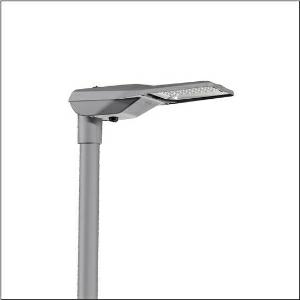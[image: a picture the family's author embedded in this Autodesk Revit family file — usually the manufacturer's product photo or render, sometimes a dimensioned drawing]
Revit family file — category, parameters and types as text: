
# Revit family: streetlight_sl_21_iq_mini___st1_0a_5xe2d41y08hb_48d2
name_source: partatom
category: Lighting Fixtures
units: mm (PartAtom-declared; Revit-internal decimal feet)

## family parameters
Cut with Voids When Loaded = No
Host = Face
Light Source = No
Part Type = Normal
Room Calculation Point = No
Round Connector Dimension = Use Diameter
Shared = No

## types (1)
- --- (1 x LED, 10080 lm, 71 W, 4000K)
    Apparent Load = 71 VA
    CIE Flux Codes = 37 72 97 100 100
    Color Rendering = 70
    Color Temperature = 4000K
    Default Elevation = 1800 mm
    Description = Streetlight SL 21 iQ mini, mast luminaire, primary light control with lens, of PMMA, primary optical cover: cover, of toughened safety glass, transparent, light distribution: ST1.0a, light emission: direct distribution, primary light characteristic: asymmetric, installation type: post-top, side-entry, LED, High Power LED, rated luminous flux: 10.080lm, luminous efficacy: 142lm/W, light colour: 740, colour temperature: 4000K, control gear: iQ-Street Remote, D4i with power reduction, control: pre-setting: logarithmic dimming characteristic, Street-Remote, Auto-Match, Temp-Guard, Lumen-Switch, Night-Set, Smart-Wire, Light-Fading, Desk-Remote (wireless, voltage-free reading and setting of iQ features in the workshop via application-optimized NFC function/RFID function), optimised constant luminous flux control (CLO 2.0), mains connection: 220..240V, AC, 50/60Hz, start of lifetime: 71W, end of service life: 75W, reduction: 31W, luminaire housing, of diecast aluminium, powder-coated, Siteco® metallic grey (DB 702S), corrosivity category C5 mid according to DIN EN ISO 12944, please order mast flange separately, inclination adjustable: 0°, 5°, 10°, 15°, sealing non-destructively replaceable, multi-level sealing system, length: 628mm, width: 235mm, height: 110mm, mast flange for spigot size: 42mm (side-entry): 5XC10008XM4, 60/48mm (side-entry/post-top): 5XC10108XM2, 76/60mm (side-entry/post-top): 5XC10108XM1, mounting height: 4..8m, Smart Interface below and above, protection rating (complete): IP66, insulation class (complete): insulation class II (safety insulation), certification: CE, ENEC, ENEC+, VDE, impact resistance: IK10, permissible operating ambient temperature for outdoor applications: -40..+50°C, standard-compliant lighting for roads and squares, packaging unit: 1 piece

Light Distribution: ST1.0a
    Height = 110 mm
    Lamp = 1 x LED
    Lamp Light Flux = 10080 lm
    Lamp Power = 71 W
    Lamp count = 1
    Length = 625 mm
    Luminous efficacy = 142 lm/W
    Manufacturer = Siteco
    ModVariant = No
    Model = 5XE2D41Y08HB
    Number of Poles = 1
    OnlyDefault = Yes
    Power Factor = 1
    Product Name = Streetlight SL 21 iQ mini | ST1.0a
    Product group = mast luminaire | pylon top
    ProductGroupID = 6100
    Protection Class = Protection class II
    Protection Degree = IP 66
    RLX_Detail_Level = 1
    RLX_Emergency_Light_Flux = 0 lm
    RLX_Emergency_Type = 0
    RLX_Emergency_Type_DB = No
    RlxData = <blob elided: 93861 chars, md5=0525dd88>
    Socket = socket
    Standby Power = 0 W
    System Light Flux = 10080 lm
    System Power = 71 W
    Type Comments = factory setting: luminous flux: 100 % | dim-lin: 254 | 716 mA
    Type Image = l_1003514.jpg
    URL = http://relux.com
    VarID = @adj_136197
    Voltage = 0 V
    Weight = 0.00 kg
    Width = 234 mm

## geometry (parser evidence)
native form markers: Blend x4, Sweep x12
no freeform markers — native parametric forms only
